# Revit family: PRD_FrankeWS_ShwrFttngsPckg_BentOutlet_ACXX2005_ACXX2006
name_source: partatom
category: Specialty Equipment
revit_build: Autodesk Revit 2018 (Build: 20190510_1515(x64)
units: mm (PartAtom-declared; Revit-internal decimal feet)

## family parameters
Cut with Voids When Loaded = Yes
Host = Face
OmniClass Number = 23.45.05.00
OmniClass Title = Sanitary Equipment
Part Type = Normal
Room Calculation Point = No
Round Connector Dimension = Use Diameter
Shared = Yes

## types (2) — shared parameters
AssetType = Fixed
Category = Pr_40_20_87_75, Shower fittings package
Default Elevation = 2000 mm  [stored 6.56168 ft]
DiameterNominal = 15  [stored 0.0492126 ft]
DurationUnit = year
Finish = chromium-plated
IfcExportAs = IfcSanitaryTerminalType
IfcExportType = USERDEFINED
Manufacturer = KWC Group AG
ManufacturerName = KWC Group AG
ManufacturerURL = www.kwc.com
Material = brass
NBSDescription = Shower fittings package
NBSReference = 45-35-70/330
NominalHeight = 55 mm  [stored 0.180446 ft]
OutletMaterial = PRD_AR_ChromatedBrass_HighPolished
ProductInformation = https://pim.kwc.com
Status = New
TypeOfShowerPipe = Bent outlet
URL = www.kwc.com
Uniclass2015Code = Pr_40_20_87_75
Uniclass2015Title = Shower fittings package
Uniclass2015Version = Products v1.23
Version = 1
WarrantyDurationUnit = year
zero-valued in all types: NominalDepth, NominalLength, NominalWidth

## per-type parameters (varying)
| type | BIMObjectName | Description | Features | GrossWeight | LengthMax | ModelNumber | Name | NetWeight | ProductCode | Size |
| ACXX2005 | PRD_AR_ShowerFittingsPackage_BentOutlet_ACXX2005 | Bent outlet 120 x 150 mm, with reduction nipple G 1/2 B and 2 pinch union nuts G 3/4 x 18 mm. Chromium-plated brass. | Maximum mounting dimension 130 x 134 mm | 0.26 kg | 150 mm | 2030050434 | Bent outlet ACXX2005 | 0.25 kg |  | 120 x 150 mm |
| ACXX2006 | PRD_AR_ShowerFittingsPackage_BentOutlet_ACXX2006 | Bent outlet 120 x 500 mm, with reduction nipple G 1/2 B and 2 pinch union nuts G 3/4 x 18 mm. Chromium-plated brass. | Maximum mounting dimension 130 x 484 mm | 0.45 kg | 500 mm  [stored 1.64042 ft] | 2030050435 | Bent outlet ACXX2006 | 0.40 kg | 210.0601.854 | 120 x 500 mm |

note: column(s) folded — value = type name in every type: Model, ModelReference

note: [stored X ft] marks values corroborated as IEEE doubles in the binary element streams (Revit-internal decimal feet)

## geometry (parser evidence)
native form markers: Sweep x2
no freeform markers — native parametric forms only
